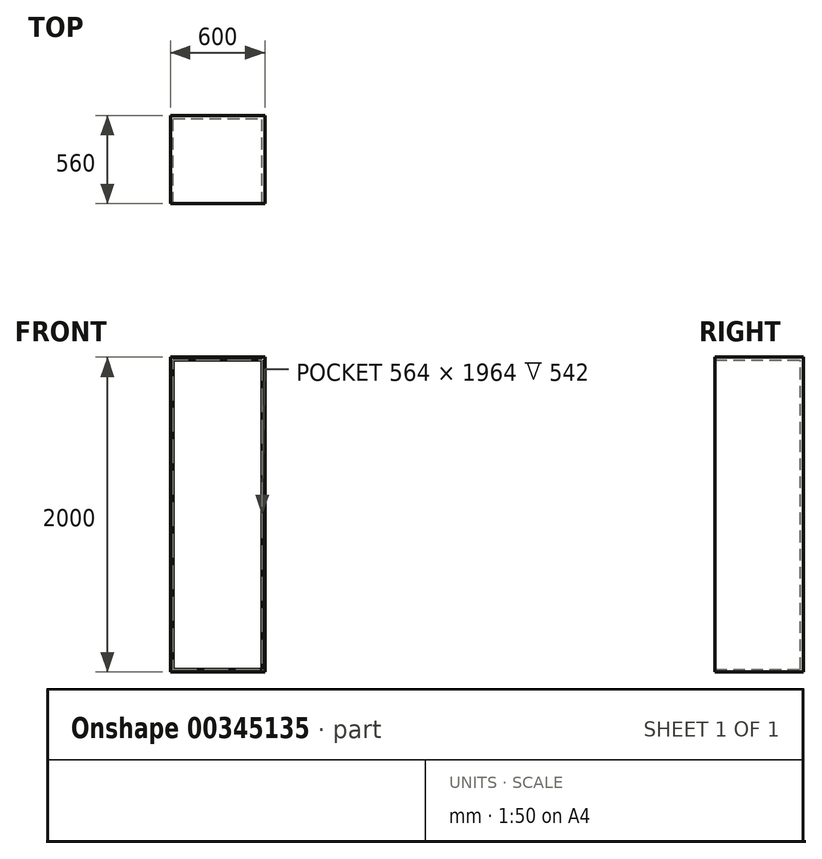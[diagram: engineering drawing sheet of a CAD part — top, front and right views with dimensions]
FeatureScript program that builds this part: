
annotation { "Feature Type Name" : "Feature", "Feature Type Description" : "" }
export const myFeature = defineFeature(function(context is Context, id is Id, definition is map)
    precondition{}
    {
        {
            var Q0;
            Q0=qCreatedBy(makeId("Front.planeOp"),FACE);
            var sketch = newSketch(context, id + "F0", { "sketchPlane" : qUnion([Q0])});
            skLineSegment(sketch, "E0.bottom", {"start": v(0, 0) * mm, "end": v(41.7, 0) * mm});
            skLineSegment(sketch, "E0.top", {"start": v(0, 40.33) * mm, "end": v(41.7, 40.33) * mm});
            skLineSegment(sketch, "E0.left", {"start": v(0, 0) * mm, "end": v(0, 40.33) * mm});
            skLineSegment(sketch, "E0.right", {"start": v(41.7, 0) * mm, "end": v(41.7, 40.33) * mm});
            skSolve(sketch);
        }
        {
            var Q0;
            Q0=makeQuery(id+"F0.imprint","IMPRINT",FACE,{"disambiguationData":[TD([[makeQuery(id+"F0.imprint","IMPRINT",EDGE,{"derivedFrom":sQuery(id+"F0.wireOp",EDGE,"E0.bottom")}),1.0]])]});
            extrude(context, id + "F1", {"entities" : qUnion([Q0]), "depth" : 560 * mm});
        }
        {
            var Q0;
            Q0=makeQuery(id+"F1.opExtrude","SWEPT_FACE",FACE,{"disambiguationData":[OSD([sQuery(id+"F0.wireOp",EDGE,"E0.left")])]});
            extrude(context, id + "F2", {"entities" : qUnion([Q0]), "operationType" : NewBodyOperationType.ADD, "oppositeDirection" : true, "depth" : 600 * mm});
        }
        {
            var Q0;
            {var subQ0=sQuery(id+"F0.wireOp",EDGE,"E0.bottom");Q0=makeQuery(id+"F2.boolean.opBoolean","MERGE",FACE,{"derivedFrom":[makeQuery(id+"F1.opExtrude","SWEPT_FACE",FACE,{"disambiguationData":[OSD([subQ0])]}),makeQuery(id+"F2.opExtrude","SWEPT_FACE",FACE,{"disambiguationData":[OSD([subQ0,sQuery(id+"F0.wireOp",EDGE,"E0.left")])]})]});}
            extrude(context, id + "F3", {"entities" : qUnion([Q0]), "operationType" : NewBodyOperationType.ADD, "oppositeDirection" : true, "depth" : 2000 * mm});
        }
        {
            var Q0;
            {var subQ0=sQuery(id+"F0.wireOp",EDGE,"E0.left");var subQ1=sQuery(id+"F0.wireOp",EDGE,"E0.bottom");Q0=makeQuery(id+"F3.boolean.opBoolean","MERGE",FACE,{"derivedFrom":[makeQuery(id+"F2.boolean.opBoolean","MERGE",FACE,{"derivedFrom":[makeQuery(id+"F1.opExtrude","CAP_FACE",FACE,{"disambiguationData":[OSD([subQ1,sQuery(id+"F0.wireOp",EDGE,"E0.top"),subQ0,sQuery(id+"F0.wireOp",EDGE,"E0.right")])],"isStart":false}),makeQuery(id+"F2.opExtrude","SWEPT_FACE",FACE,{"disambiguationData":[OSD([subQ0]),TDD([makeQuery(id+"F1.opExtrude","CAP_EDGE",EDGE,{"disambiguationData":[OSD([subQ0])],"isStart":false})])]})]}),makeQuery(id+"F3.opExtrude","SWEPT_FACE",FACE,{"disambiguationData":[OSD([subQ1,subQ0]),TDD([makeQuery(id+"F2.boolean.opBoolean","MERGE",EDGE,{"derivedFrom":[makeQuery(id+"F1.opExtrude","CAP_EDGE",EDGE,{"disambiguationData":[OSD([subQ1])],"isStart":false}),makeQuery(id+"F2.opExtrude","SWEPT_EDGE",EDGE,{"disambiguationData":[OSD([subQ1,subQ0]),TDD([makeQuery(id+"F1.opExtrude","CAP_VERTEX",VERTEX,{"disambiguationData":[OSD([subQ1,subQ0])],"isStart":false})])]})]})])]})]});}
            shell(context, id + "F4", {"entities" : qUnion([Q0]), "thickness" : 18 * mm});
        }
    });
